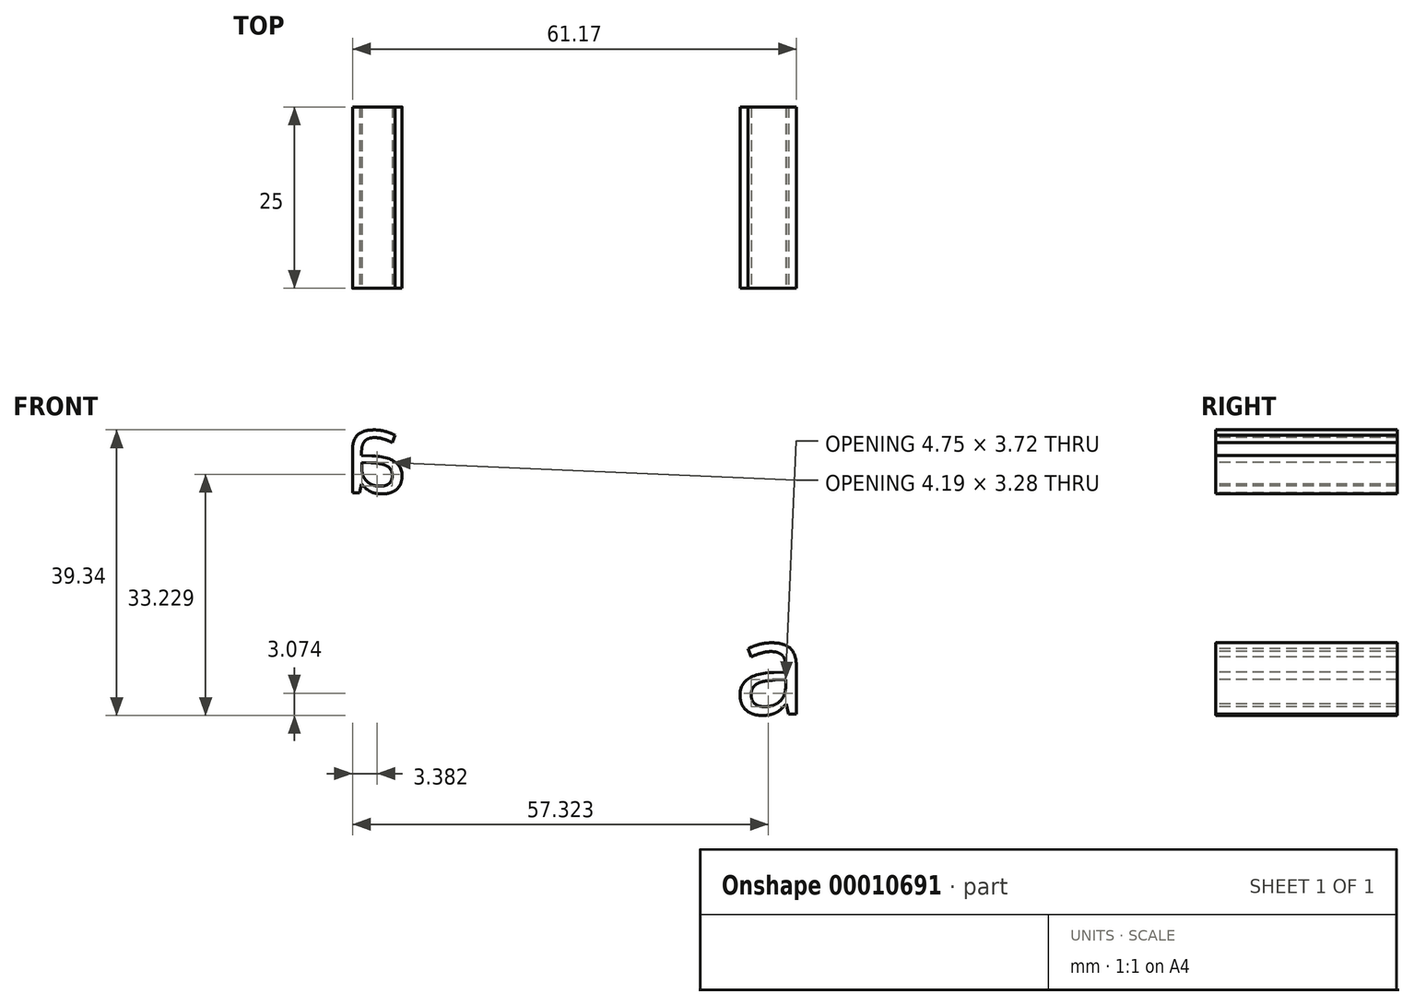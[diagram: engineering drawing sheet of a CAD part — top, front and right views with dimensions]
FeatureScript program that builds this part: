
annotation { "Feature Type Name" : "Feature", "Feature Type Description" : "" }
export const myFeature = defineFeature(function(context is Context, id is Id, definition is map)
    precondition{}
    {
        {
            var Q0;
            Q0=qCreatedBy(makeId("Front.planeOp"),FACE);
            var sketch = newSketch(context, id + "F0", { "sketchPlane" : qUnion([Q0])});
            skLineSegment(sketch, "E0", {"start": v(0, 0) * mm, "end": v(0, 31.42) * mm});
            skText(sketch, "E1", { "text": "a", "fontName": "OpenSans-Regular.ttf"});
            const initialGuessF0  = {"E1": [0.01984, 0.0077, 1, 0, 0.01301]};
            skSetInitialGuess(sketch, initialGuessF0);
            skSolve(sketch);
        }
        {
            var Q0;
            Q0=sQuery(id+"F0.wireOp",EDGE,"E0");
            cPlane(context, id + "F1", {"entities" : qUnion([Q0]), "cplaneType" : CPlaneType.LINE_ANGLE, "offset" : 150 * mm, "angle" : 90 * degree, "width" : 150 * mm, "height" : 150 * mm});
        }
        {
            var Q0;
            Q0=qCreatedBy(id+"F1.planeOp",FACE);
            var sketch = newSketch(context, id + "F2", { "sketchPlane" : qUnion([Q0])});
            skText(sketch, "E2", { "text": "a\n", "fontName": "OpenSans-Regular.ttf"});
            const initialGuessF2  = {"E2": [0.02518, 0.0382, 1, 0, 0.01146]};
            skSetInitialGuess(sketch, initialGuessF2);
            skSolve(sketch);
        }
        {
            var Q0;
            Q0 = qSketchRegion(id + "F2", true);
            var Q1;
            Q1 = qSketchRegion(id + "F0", true);
            extrude(context, id + "F3", {"entities" : qUnion([Q0, Q1]), "depth" : 25 * mm});
        }
    });
